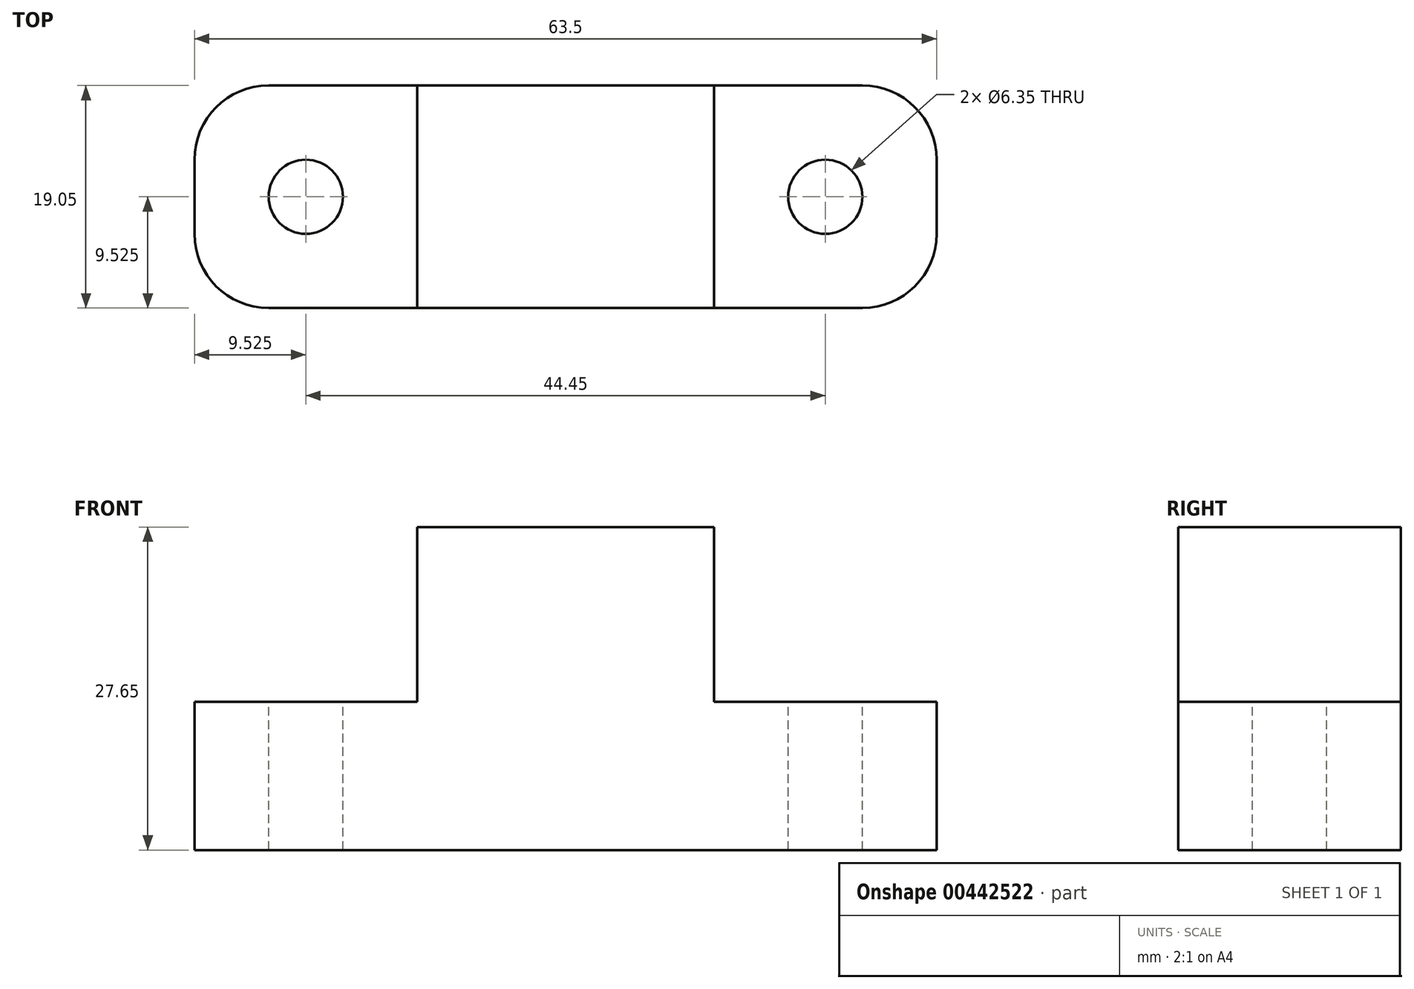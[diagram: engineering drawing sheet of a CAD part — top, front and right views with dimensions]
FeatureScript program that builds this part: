
annotation { "Feature Type Name" : "Feature", "Feature Type Description" : "" }
export const myFeature = defineFeature(function(context is Context, id is Id, definition is map)
    precondition{}
    {
        {
            var Q0;
            Q0=qCreatedBy(makeId("Front.planeOp"),FACE);
            var sketch = newSketch(context, id + "F0", { "sketchPlane" : qUnion([Q0])});
            skLineSegment(sketch, "E0.bottom", {"start": v(0, 0) * mm, "end": v(-19.05, 0) * mm});
            skLineSegment(sketch, "E0.top", {"start": v(0, 12.7) * mm, "end": v(-19.05, 12.7) * mm});
            skLineSegment(sketch, "E0.right", {"start": v(-19.05, 0) * mm, "end": v(-19.05, 12.7) * mm});
            skLineSegment(sketch, "E1", {"start": v(0, 12.7) * mm, "end": v(0, 27.65) * mm});
            skLineSegment(sketch, "E2", {"start": v(0, 27.65) * mm, "end": v(12.7, 27.65) * mm});
            skLineSegment(sketch, "E3", {"start": v(12.7, 27.65) * mm, "end": v(12.7, 0) * mm});
            skLineSegment(sketch, "E4", {"start": v(12.7, 0) * mm, "end": v(0, 0) * mm});
            skSolve(sketch);
        }
        {
            var Q0;
            Q0=makeQuery(id+"F0.imprint","IMPRINT",FACE,{"disambiguationData":[TD([[makeQuery(id+"F0.imprint","IMPRINT",EDGE,{"derivedFrom":sQuery(id+"F0.wireOp",EDGE,"E0.bottom")}),-1.0]])]});
            extrude(context, id + "F1", {"entities" : qUnion([Q0]), "depth" : 19.05 * mm});
        }
        {
            var Q0;
            Q0=makeQuery(id+"F1.opExtrude","SWEPT_FACE",FACE,{"disambiguationData":[OSD([sQuery(id+"F0.wireOp",EDGE,"E0.top")])]});
            var sketch = newSketch(context, id + "F2", { "sketchPlane" : qUnion([Q0])});
            skPoint(sketch, "E5", {"position": v(-9.53, -9.53) * mm});
            skSolve(sketch);
        }
        {
            var Q0;
            Q0=sQuery(id+"F2.wireOp",VERTEX,"E5");
            var Q1;
            Q1=makeQuery(id+"F1.opExtrude","SWEPT_BODY",BODY,{"disambiguationData":[OSD([sQuery(id+"F0.wireOp",EDGE,"E0.bottom"),sQuery(id+"F0.wireOp",EDGE,"E0.top"),sQuery(id+"F0.wireOp",EDGE,"E0.right"),sQuery(id+"F0.wireOp",EDGE,"E1"),sQuery(id+"F0.wireOp",EDGE,"E2"),sQuery(id+"F0.wireOp",EDGE,"E3"),sQuery(id+"F0.wireOp",EDGE,"E4")])]});
            hole(context, id + "F3", {"style" : HoleStyle.SIMPLE, "endStyle" : HoleEndStyle.THROUGH, "holeDiameter" : 6.35 * mm, "isTappedThrough" : true, "tappedDepth" : 12.7 * mm, "tapClearance" : 3, "locations" : qUnion([Q0]), "scope" : qUnion([Q1])});
        }
        {
            var Q0;
            Q0=makeQuery(id+"F1.opExtrude","CAP_EDGE",EDGE,{"disambiguationData":[OSD([sQuery(id+"F0.wireOp",EDGE,"E0.right")])],"isStart":true});
            var Q1;
            Q1=makeQuery(id+"F1.opExtrude","CAP_EDGE",EDGE,{"disambiguationData":[OSD([sQuery(id+"F0.wireOp",EDGE,"E0.right")])],"isStart":false});
            fillet(context, id + "F4", {"entities" : qUnion([Q0, Q1]), "radius" : 6.35 * mm, "tangentPropagation" : true, "allowEdgeOverflow" : false});
        }
        {
            var Q0;
            Q0=makeQuery(id+"F1.opExtrude","SWEPT_BODY",BODY,{"disambiguationData":[OSD([sQuery(id+"F0.wireOp",EDGE,"E0.bottom"),sQuery(id+"F0.wireOp",EDGE,"E0.top"),sQuery(id+"F0.wireOp",EDGE,"E0.right"),sQuery(id+"F0.wireOp",EDGE,"E1"),sQuery(id+"F0.wireOp",EDGE,"E2"),sQuery(id+"F0.wireOp",EDGE,"E3"),sQuery(id+"F0.wireOp",EDGE,"E4")])]});
            var Q1;
            Q1=makeQuery(id+"F1.opExtrude","SWEPT_FACE",FACE,{"disambiguationData":[OSD([sQuery(id+"F0.wireOp",EDGE,"E3")])]});
            mirror(context, id + "F5", {"operationType" : NewBodyOperationType.ADD, "entities" : qUnion([Q0]), "mirrorPlane" : qUnion([Q1])});
        }
    });
